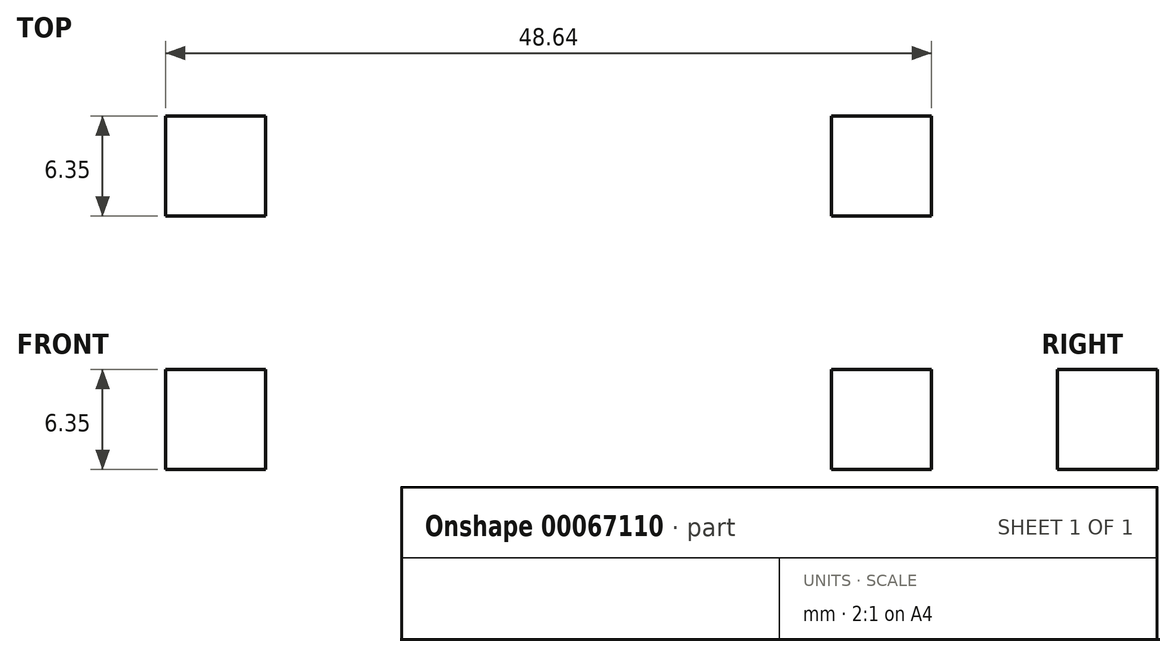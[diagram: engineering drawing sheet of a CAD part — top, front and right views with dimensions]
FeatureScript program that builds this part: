
annotation { "Feature Type Name" : "Feature", "Feature Type Description" : "" }
export const myFeature = defineFeature(function(context is Context, id is Id, definition is map)
    precondition{}
    {
        {
            var Q0;
            Q0=qCreatedBy(makeId("Top.planeOp"),FACE);
            var sketch = newSketch(context, id + "F0", { "sketchPlane" : qUnion([Q0])});
            skLineSegment(sketch, "E0.bottom", {"start": v(-24.33, 0) * mm, "end": v(24.32, 0) * mm});
            skLineSegment(sketch, "E0.top", {"start": v(-24.33, -48.65) * mm, "end": v(24.33, -48.65) * mm});
            skLineSegment(sketch, "E0.left", {"start": v(-24.33, 0) * mm, "end": v(-24.32, -48.65) * mm});
            skLineSegment(sketch, "E0.right", {"start": v(24.32, 0) * mm, "end": v(24.32, -48.65) * mm});
            skLineSegment(sketch, "E1.bottom", {"start": v(17.98, 0) * mm, "end": v(24.32, 0) * mm});
            skLineSegment(sketch, "E1.top", {"start": v(17.98, -6.35) * mm, "end": v(24.32, -6.35) * mm});
            skLineSegment(sketch, "E1.left", {"start": v(17.98, 0) * mm, "end": v(17.98, -6.35) * mm});
            skLineSegment(sketch, "E1.right", {"start": v(24.32, 0) * mm, "end": v(24.32, -6.35) * mm});
            skLineSegment(sketch, "E2.right", {"start": v(-17.98, 0) * mm, "end": v(-17.98, -6.35) * mm});
            skLineSegment(sketch, "E2.left", {"start": v(-24.32, 0) * mm, "end": v(-24.32, -6.35) * mm});
            skLineSegment(sketch, "E2.top", {"start": v(-24.32, -6.35) * mm, "end": v(-17.98, -6.35) * mm});
            skLineSegment(sketch, "E2.bottom", {"start": v(-24.33, 0) * mm, "end": v(-17.98, 0) * mm});
            skLineSegment(sketch, "E3.right", {"start": v(-17.98, -42.3) * mm, "end": v(-17.98, -48.65) * mm});
            skLineSegment(sketch, "E3.left", {"start": v(-24.33, -42.3) * mm, "end": v(-24.33, -48.65) * mm});
            skLineSegment(sketch, "E3.top", {"start": v(-24.33, -48.65) * mm, "end": v(-17.98, -48.65) * mm});
            skLineSegment(sketch, "E3.bottom", {"start": v(-24.32, -42.3) * mm, "end": v(-17.98, -42.3) * mm});
            skLineSegment(sketch, "E4.right", {"start": v(24.32, -42.3) * mm, "end": v(24.32, -48.65) * mm});
            skLineSegment(sketch, "E4.left", {"start": v(17.98, -42.3) * mm, "end": v(17.98, -48.65) * mm});
            skLineSegment(sketch, "E4.top", {"start": v(17.98, -48.65) * mm, "end": v(24.33, -48.65) * mm});
            skLineSegment(sketch, "E4.bottom", {"start": v(17.98, -42.3) * mm, "end": v(24.32, -42.3) * mm});
            skLineSegment(sketch, "E5.bottom", {"start": v(-9, -12.32) * mm, "end": v(9, -12.32) * mm});
            skLineSegment(sketch, "E5.top", {"start": v(-9, -36.32) * mm, "end": v(9, -36.32) * mm});
            skLineSegment(sketch, "E5.left", {"start": v(-9, -12.32) * mm, "end": v(-9, -36.32) * mm});
            skLineSegment(sketch, "E5.right", {"start": v(9, -12.33) * mm, "end": v(9, -36.32) * mm});
            skLineSegment(sketch, "E6", {"start": v(-9, -12.32) * mm, "end": v(-9, 0) * mm, "construction": true});
            skLineSegment(sketch, "E7", {"start": v(-9, -36.32) * mm, "end": v(-9, -48.65) * mm, "construction": true});
            skLineSegment(sketch, "E8", {"start": v(-9, -36.32) * mm, "end": v(-24.32, -36.32) * mm, "construction": true});
            skLineSegment(sketch, "E9", {"start": v(9, -36.32) * mm, "end": v(24.32, -36.32) * mm, "construction": true});
            skSolve(sketch);
        }
        {
            var Q0;
            Q0=makeQuery(id+"F0.imprint","IMPRINT",FACE,{"disambiguationData":[TD([[makeQuery(id+"F0.imprint","IMPRINT",EDGE,{"derivedFrom":sQuery(id+"F0.wireOp",EDGE,"E0.bottom")}),-1.0]])]});
            extrude(context, id + "F1", {"entities" : qUnion([Q0]), "depth" : 6.35 * mm});
        }
    });
